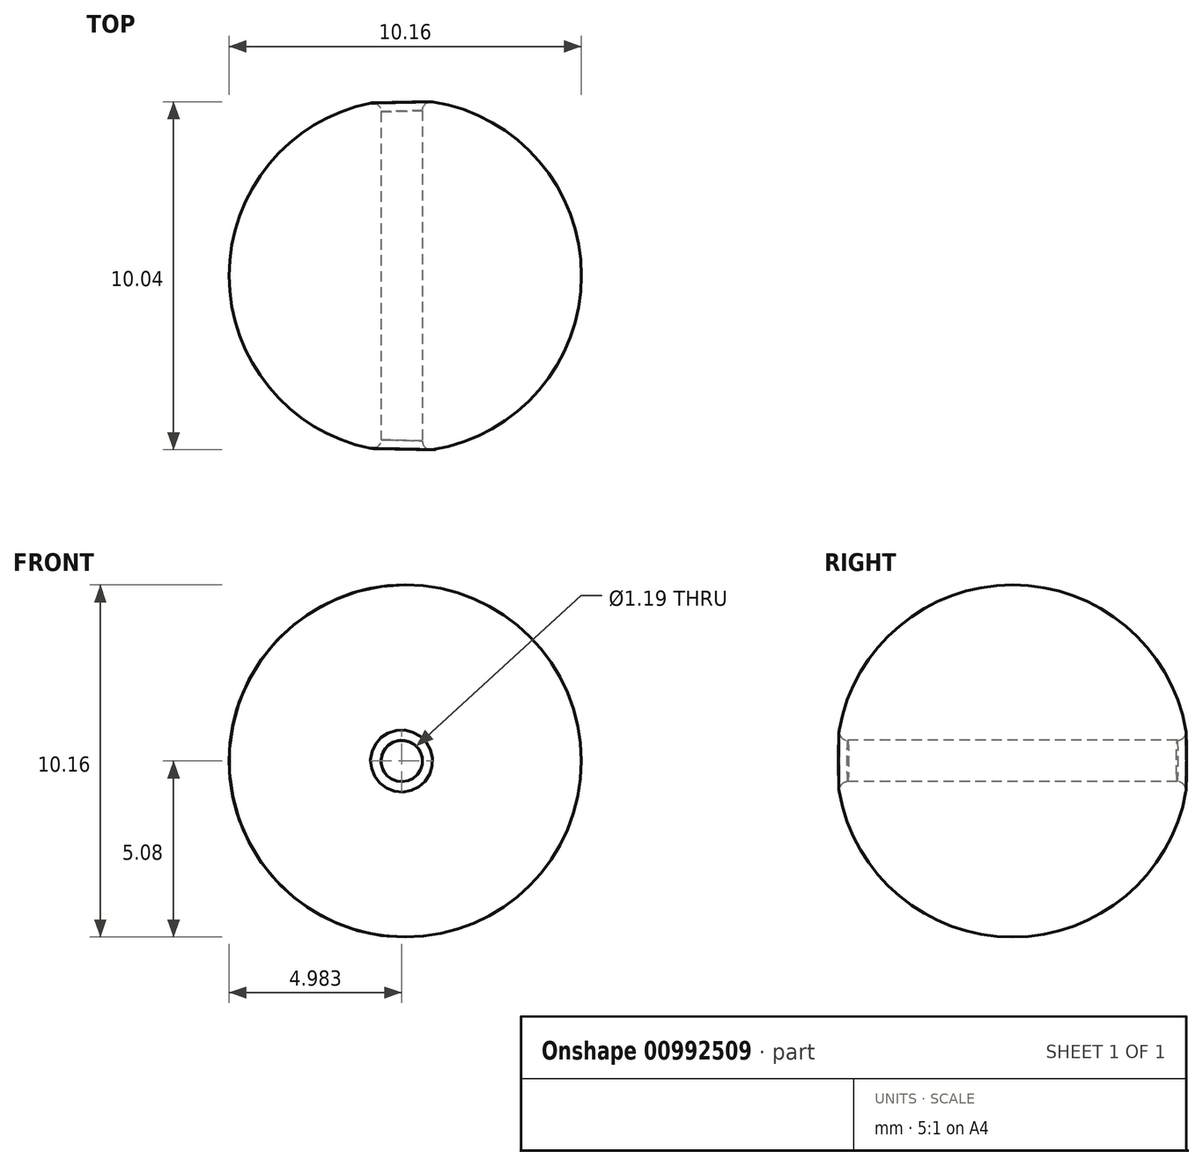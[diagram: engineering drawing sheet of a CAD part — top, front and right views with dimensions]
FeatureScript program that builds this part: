
annotation { "Feature Type Name" : "Feature", "Feature Type Description" : "" }
export const myFeature = defineFeature(function(context is Context, id is Id, definition is map)
    precondition{}
    {
        {
            var Q0;
            Q0=qCreatedBy(makeId("Top.planeOp"),FACE);
            var sketch = newSketch(context, id + "F0", { "sketchPlane" : qUnion([Q0])});
            skCircle(sketch, "E0", {"center": v(-46.1, 37.68) * mm, "radius": 5.08 * mm});
            skSolve(sketch);
        }
        {
            var Q0;
            Q0=makeQuery(id+"F0.imprint","IMPRINT",FACE,{"disambiguationData":[TD([[makeQuery(id+"F0.imprint","IMPRINT",EDGE,{"derivedFrom":sQuery(id+"F0.wireOp",EDGE,"E0")}),1.0]])]});
            extrude(context, id + "F1", {"entities" : qUnion([Q0]), "depth" : 5.08 * mm, "offsetDistance" : 25.4 * mm, "hasSecondDirection" : true, "secondDirectionOppositeDirection" : true, "secondDirectionDepth" : 5.08 * mm});
        }
        {
            var Q0;
            Q0=makeQuery(id+"F1.opExtrude","CAP_EDGE",EDGE,{"disambiguationData":[OSD([sQuery(id+"F0.wireOp",EDGE,"E0")])],"isStart":false});
            var Q1;
            Q1=makeQuery(id+"F1.opExtrude","CAP_EDGE",EDGE,{"disambiguationData":[OSD([sQuery(id+"F0.wireOp",EDGE,"E0")])],"isStart":true});
            fillet(context, id + "F2", {"entities" : qUnion([Q0, Q1]), "radius" : 5.08 * mm, "tangentPropagation" : true, "allowEdgeOverflow" : false});
        }
        {
            var Q0;
            Q0=qCreatedBy(makeId("Front.planeOp"),FACE);
            var sketch = newSketch(context, id + "F3", { "sketchPlane" : qUnion([Q0])});
            skCircle(sketch, "E1", {"center": v(-46.2, 0) * mm, "radius": 0.6 * mm});
            skSolve(sketch);
        }
        {
            var Q0;
            Q0=makeQuery(id+"F3.imprint","IMPRINT",FACE,{"disambiguationData":[TD([[makeQuery(id+"F3.imprint","IMPRINT",EDGE,{"derivedFrom":sQuery(id+"F3.wireOp",EDGE,"E1")}),1.0]])]});
            extrude(context, id + "F4", {"entities" : qUnion([Q0]), "operationType" : NewBodyOperationType.REMOVE, "oppositeDirection" : true, "depth" : 49.2 * mm, "offsetDistance" : 25.4 * mm});
        }
        {
            var Q0;
            Q0=makeQuery(id+"F4.boolean.opBoolean","INTERSECT",EDGE,{"disambiguationData":[OD(0.0)],"derivedFrom":[makeQuery(id+"F2.opFillet","BLEND_FACE",FACE,{"disambiguationData":[OSD([sQuery(id+"F0.wireOp",EDGE,"E0")])]}),makeQuery(id+"F4.opExtrude","SWEPT_FACE",FACE,{"disambiguationData":[OSD([sQuery(id+"F3.wireOp",EDGE,"E1")])]})]});
            fillet(context, id + "F5", {"entities" : qUnion([Q0]), "radius" : 0.25 * mm, "tangentPropagation" : true, "allowEdgeOverflow" : false});
        }
        {
            var Q0;
            Q0=makeQuery(id+"F4.boolean.opBoolean","INTERSECT",EDGE,{"disambiguationData":[OD(1.0)],"derivedFrom":[makeQuery(id+"F2.opFillet","BLEND_FACE",FACE,{"disambiguationData":[OSD([sQuery(id+"F0.wireOp",EDGE,"E0")])]}),makeQuery(id+"F4.opExtrude","SWEPT_FACE",FACE,{"disambiguationData":[OSD([sQuery(id+"F3.wireOp",EDGE,"E1")])]})]});
            fillet(context, id + "F6", {"entities" : qUnion([Q0]), "radius" : 0.25 * mm, "tangentPropagation" : true, "allowEdgeOverflow" : false});
        }
    });
